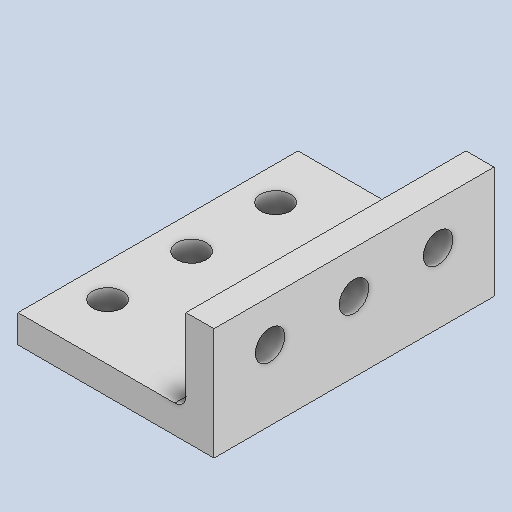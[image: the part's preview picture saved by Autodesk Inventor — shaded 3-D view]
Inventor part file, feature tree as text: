
AUTODESK INVENTOR PART (.ipt)
format: ipt  version: 2022 (Build 260153000, 153)  size: 124,416 bytes
history: native  units: in
note: dims shown in document units (in); Inventor stores cm internally (conversion verified against a paired STEP export)
features: other x3, sketch x3
ambient origin geometry x8: Origin, YZ Plane, XZ Plane, XY Plane, X Axis, Y Axis, Z Axis, Center Point
bodies: Solid1 (feature_tree)
feature tree (6):
  other  "Linear Rail Frame Bracket.ipt"
  other  "Solid1::Linear Rail Frame Bracket.ipt"
  other  "TaggingFeature1"
  sketch  "Sketch1"  dims[d0=0.3937in]
  sketch  "Sketch2"
  sketch  "Sketch3"
